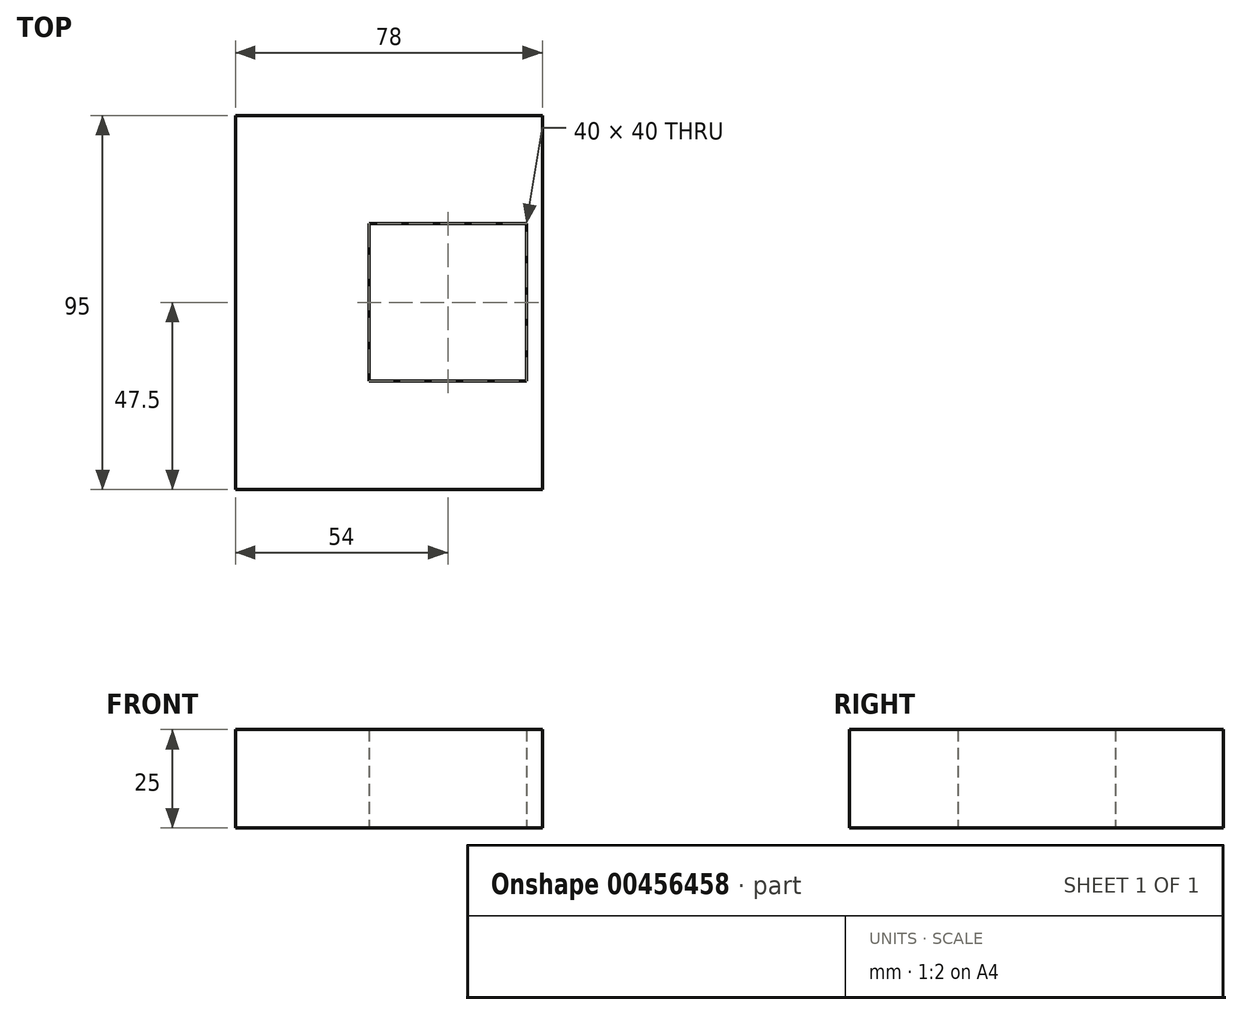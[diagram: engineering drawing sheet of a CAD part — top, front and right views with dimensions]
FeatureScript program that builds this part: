
annotation { "Feature Type Name" : "Feature", "Feature Type Description" : "" }
export const myFeature = defineFeature(function(context is Context, id is Id, definition is map)
    precondition{}
    {
        {
            var Q0;
            Q0=qCreatedBy(makeId("Top.planeOp"),FACE);
            var sketch = newSketch(context, id + "F0", { "sketchPlane" : qUnion([Q0])});
            skLineSegment(sketch, "E0.bottom", {"start": v(39, -47.5) * mm, "end": v(-39, -47.5) * mm});
            skLineSegment(sketch, "E0.top", {"start": v(39, 47.5) * mm, "end": v(-39, 47.5) * mm});
            skLineSegment(sketch, "E0.left", {"start": v(39, -47.5) * mm, "end": v(39, 47.5) * mm});
            skLineSegment(sketch, "E0.right", {"start": v(-39, -47.5) * mm, "end": v(-39, 47.5) * mm});
            skPoint(sketch, "E0.middle", {"position": v(0, 0) * mm});
            skLineSegment(sketch, "E1.bottom", {"start": v(35, -20) * mm, "end": v(-5, -20) * mm});
            skLineSegment(sketch, "E1.top", {"start": v(35, 20) * mm, "end": v(-5, 20) * mm});
            skLineSegment(sketch, "E1.left", {"start": v(35, -20) * mm, "end": v(35, 20) * mm});
            skLineSegment(sketch, "E1.right", {"start": v(-5, -20) * mm, "end": v(-5, 20) * mm});
            skPoint(sketch, "E1.middle", {"position": v(15, 0) * mm});
            skSolve(sketch);
        }
        {
            var Q0;
            Q0=makeQuery(id+"F0.imprint","IMPRINT",FACE,{"disambiguationData":[TD([[makeQuery(id+"F0.imprint","IMPRINT",EDGE,{"derivedFrom":sQuery(id+"F0.wireOp",EDGE,"E0.bottom")}),-1.0]])]});
            extrude(context, id + "F1", {"entities" : qUnion([Q0]), "depth" : 25 * mm});
        }
    });
